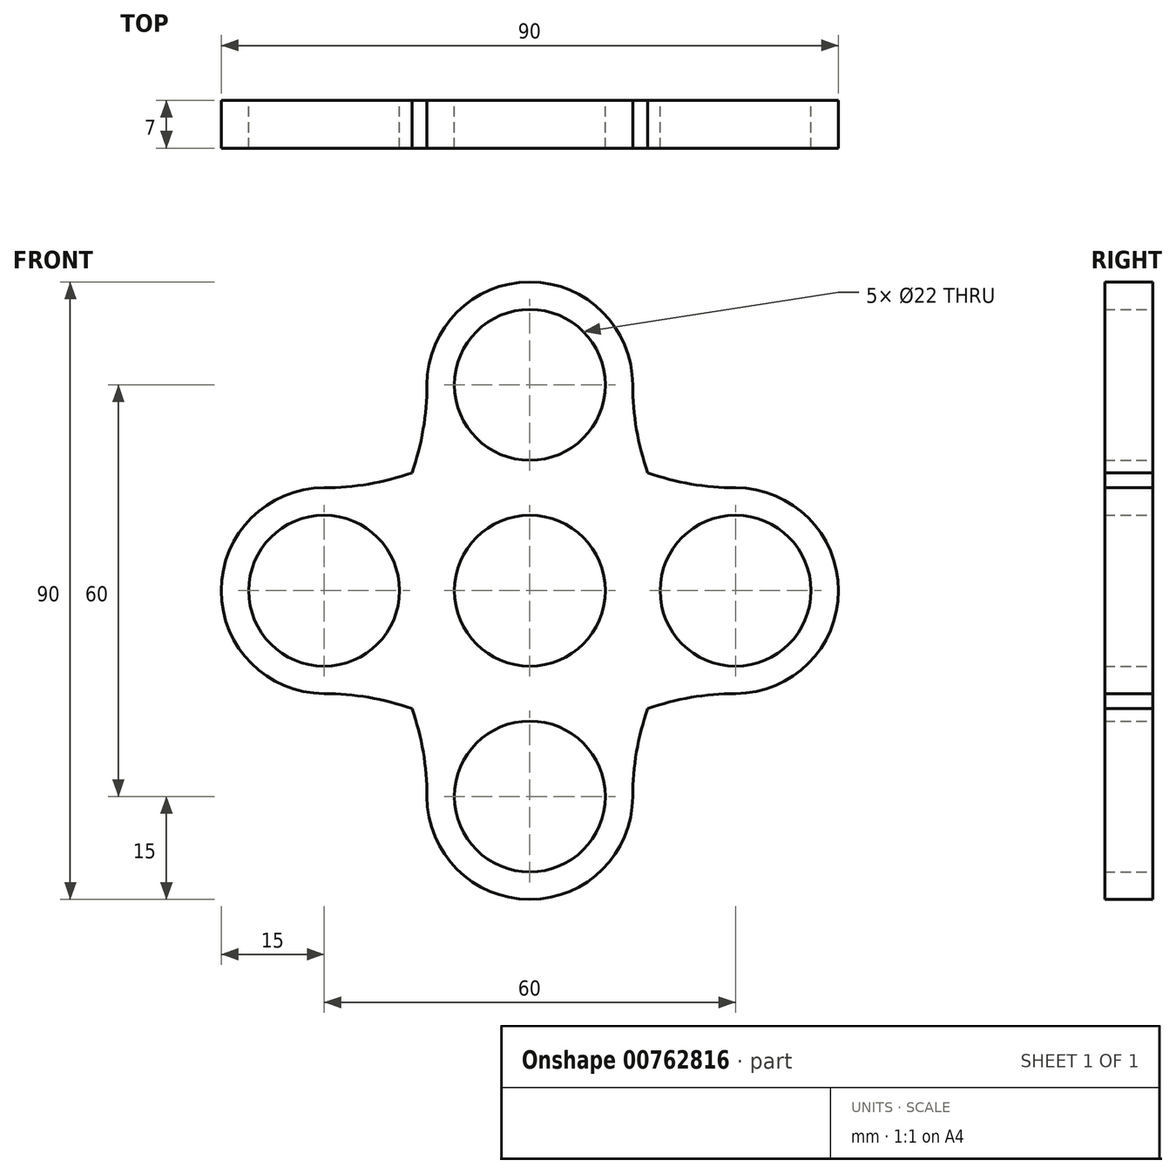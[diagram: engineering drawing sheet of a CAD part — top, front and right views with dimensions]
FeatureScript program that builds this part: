
annotation { "Feature Type Name" : "Feature", "Feature Type Description" : "" }
export const myFeature = defineFeature(function(context is Context, id is Id, definition is map)
    precondition{}
    {
        {
            var Q0;
            Q0=qCreatedBy(makeId("Front.planeOp"),FACE);
            var sketch = newSketch(context, id + "F0", { "sketchPlane" : qUnion([Q0])});
            skCircle(sketch, "E0", {"center": v(0, 0) * mm, "radius": 11 * mm});
            skLineSegment(sketch, "E1", {"start": v(0, 0) * mm, "end": v(0, 30) * mm});
            skLineSegment(sketch, "E2", {"start": v(0, 0) * mm, "end": v(0, -30) * mm});
            skLineSegment(sketch, "E3", {"start": v(0, 0) * mm, "end": v(-30, 0) * mm});
            skLineSegment(sketch, "E4", {"start": v(0, 0) * mm, "end": v(30, 0) * mm});
            skCircle(sketch, "E5", {"center": v(0, 30) * mm, "radius": 11 * mm});
            skCircle(sketch, "E6", {"center": v(30, 0) * mm, "radius": 11 * mm});
            skCircle(sketch, "E7", {"center": v(-30, 0) * mm, "radius": 11 * mm});
            skCircle(sketch, "E8", {"center": v(0, -30) * mm, "radius": 11 * mm});
            skArc(sketch, "E9", {"start": v(30, 15) * mm, "mid": v(45, 0) * mm, "end": v(30, -15) * mm});
            skArc(sketch, "E10", {"start": v(15, -30) * mm, "mid": v(0, -45) * mm, "end": v(-15, -30) * mm});
            skArc(sketch, "E11", {"start": v(-30, -15) * mm, "mid": v(-45, 0) * mm, "end": v(-30, 15) * mm});
            skArc(sketch, "E12", {"start": v(-15, 30) * mm, "mid": v(0, 45) * mm, "end": v(15, 30) * mm});
            skLineSegment(sketch, "E13", {"start": v(11, 0) * mm, "end": v(0, -11) * mm});
            skArc(sketch, "E14", {"start": v(-15, 30) * mm, "mid": v(-14.2, 25.94) * mm, "end": v(-11.9, 22.5) * mm});
            skArc(sketch, "E15", {"start": v(-30, 15) * mm, "mid": v(-25.94, 14.2) * mm, "end": v(-22.5, 11.9) * mm});
            skArc(sketch, "E16", {"start": v(-30, -15) * mm, "mid": v(-25.94, -14.2) * mm, "end": v(-22.5, -11.9) * mm});
            skArc(sketch, "E17", {"start": v(-15, -30) * mm, "mid": v(-14.2, -25.94) * mm, "end": v(-11.9, -22.5) * mm});
            skArc(sketch, "E18", {"start": v(15, -30) * mm, "mid": v(14.2, -25.94) * mm, "end": v(11.9, -22.5) * mm});
            skArc(sketch, "E19", {"start": v(30, -15) * mm, "mid": v(25.94, -14.2) * mm, "end": v(22.5, -11.9) * mm});
            skArc(sketch, "E20", {"start": v(30, 15) * mm, "mid": v(25.94, 14.2) * mm, "end": v(22.5, 11.9) * mm});
            skArc(sketch, "E21", {"start": v(15, 30) * mm, "mid": v(14.2, 25.94) * mm, "end": v(11.9, 22.5) * mm});
            skArc(sketch, "E22", {"start": v(15, 30) * mm, "mid": v(15.55, 23.5) * mm, "end": v(17.2, 17.2) * mm});
            skArc(sketch, "E23", {"start": v(30, 15) * mm, "mid": v(23.5, 15.55) * mm, "end": v(17.2, 17.2) * mm});
            skArc(sketch, "E24", {"start": v(30, -15) * mm, "mid": v(23.5, -15.55) * mm, "end": v(17.2, -17.2) * mm});
            skArc(sketch, "E25", {"start": v(15, -30) * mm, "mid": v(15.55, -23.5) * mm, "end": v(17.2, -17.2) * mm});
            skArc(sketch, "E26", {"start": v(-15, -30) * mm, "mid": v(-15.55, -23.5) * mm, "end": v(-17.2, -17.2) * mm});
            skArc(sketch, "E27", {"start": v(-30, -15) * mm, "mid": v(-23.5, -15.55) * mm, "end": v(-17.2, -17.2) * mm});
            skArc(sketch, "E28", {"start": v(-15, 30) * mm, "mid": v(-15.55, 23.5) * mm, "end": v(-17.2, 17.2) * mm});
            skArc(sketch, "E29", {"start": v(-30, 15) * mm, "mid": v(-23.5, 15.55) * mm, "end": v(-17.2, 17.2) * mm});
            skSolve(sketch);
        }
        {
            var Q0;
            Q0=makeQuery(id+"F0.imprint","IMPRINT",FACE,{"disambiguationData":[TD([[makeQuery(id+"F0.imprint","IMPRINT",EDGE,{"derivedFrom":sQuery(id+"F0.wireOp",EDGE,"E5")}),-1.0]])]});
            extrude(context, id + "F1", {"entities" : qUnion([Q0]), "depth" : 7 * mm, "offsetDistance" : 25 * mm});
        }
    });
